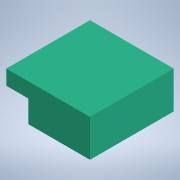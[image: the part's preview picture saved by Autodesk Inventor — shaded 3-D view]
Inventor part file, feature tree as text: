
AUTODESK INVENTOR PART (.ipt)
format: ipt  version: 2022.3 (Build 263350000, 350)  size: 109,568 bytes
history: native  units: in
note: dims shown in document units (in); Inventor stores cm internally (conversion verified against a paired STEP export)
features: extrude x2, sketch x2
ambient origin geometry x8: Origin, YZ Plane, XZ Plane, XY Plane, X Axis, Y Axis, Z Axis, Center Point
bodies: Solid1 (feature_tree)
feature tree (4):
  extrude  "Extrusion1"  Depth=11.3in
  extrude  "Extrusion2"  Depth=3.0in
  sketch  "Sketch1"  dims[d0=11.3in d1=11.3in]
  sketch  "Sketch2"  dims[d2=5.0in d3=0.0in d4=3.0in d5=3.0in d6=0.0in]
